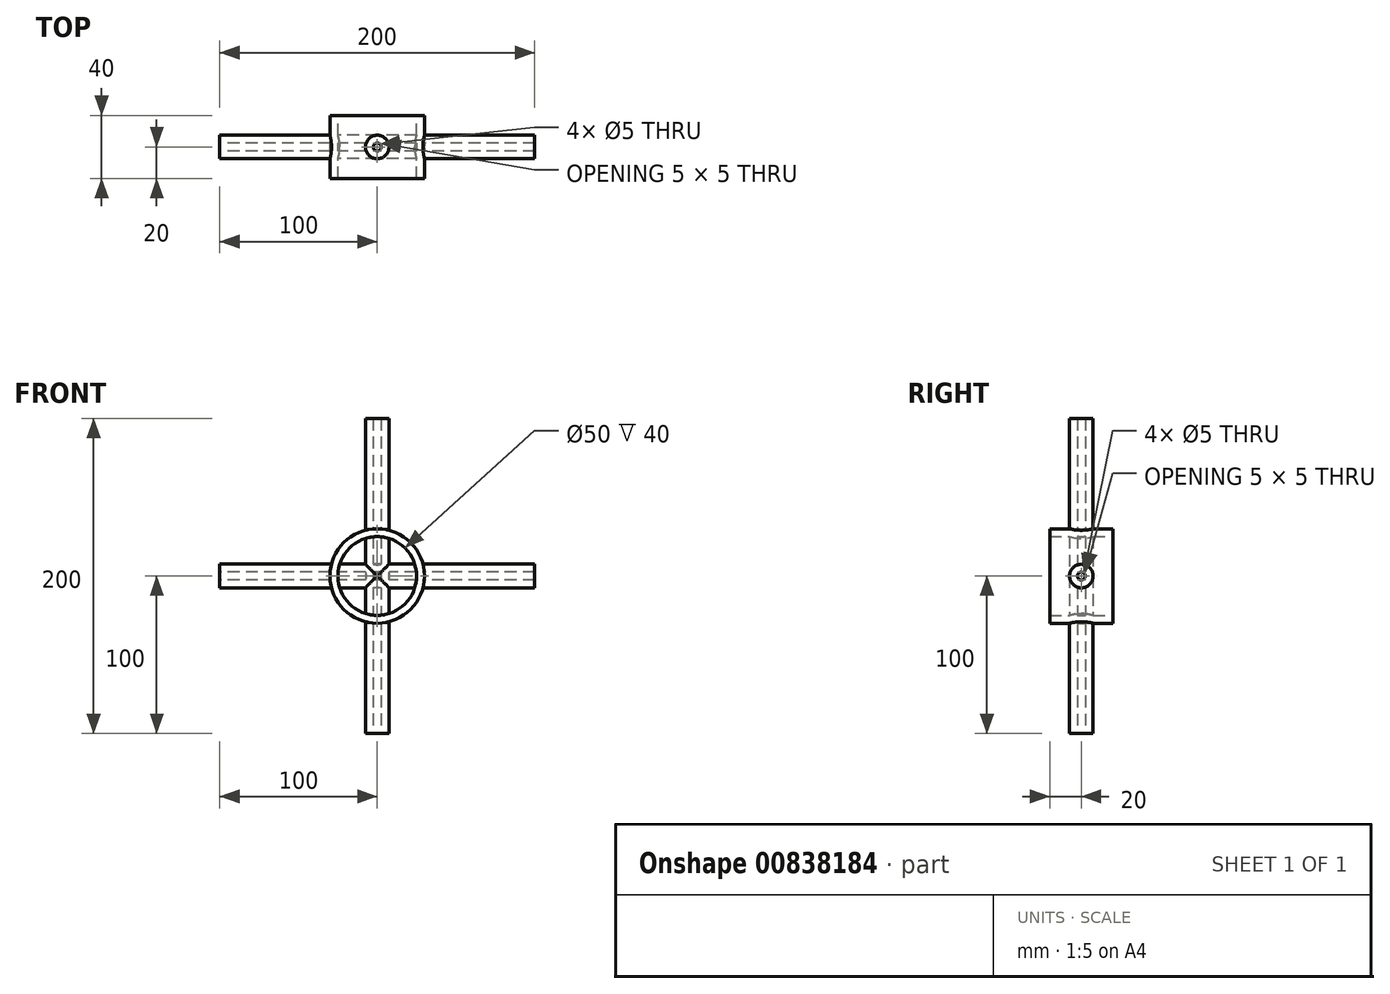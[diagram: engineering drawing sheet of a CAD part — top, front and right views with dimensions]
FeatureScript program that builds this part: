
annotation { "Feature Type Name" : "Feature", "Feature Type Description" : "" }
export const myFeature = defineFeature(function(context is Context, id is Id, definition is map)
    precondition{}
    {
        {
            var Q0;
            Q0=qCreatedBy(makeId("Front.planeOp"),FACE);
            var sketch = newSketch(context, id + "F0", { "sketchPlane" : qUnion([Q0])});
            skCircle(sketch, "E0", {"center": v(0, 0) * mm, "radius": 30 * mm});
            skCircle(sketch, "E1", {"center": v(0, 0) * mm, "radius": 25 * mm});
            skSolve(sketch);
        }
        {
            var Q0;
            Q0 = qSketchRegion(id + "F0", true);
            extrude(context, id + "F1", {"entities" : qUnion([Q0]), "endBound" : BoundingType.SYMMETRIC, "depth" : 40 * mm, "offsetDistance" : 25.4 * mm});
        }
        {
            var Q0;
            Q0=qCreatedBy(makeId("Top.planeOp"),FACE);
            var sketch = newSketch(context, id + "F2", { "sketchPlane" : qUnion([Q0])});
            skCircle(sketch, "E2", {"center": v(0, 0) * mm, "radius": 7.5 * mm});
            skCircle(sketch, "E3", {"center": v(0, 0) * mm, "radius": 2.5 * mm});
            skSolve(sketch);
        }
        {
            var Q0;
            Q0=makeQuery(id+"F2.imprint","IMPRINT",FACE,{"disambiguationData":[TD([[makeQuery(id+"F2.imprint","IMPRINT",EDGE,{"derivedFrom":sQuery(id+"F2.wireOp",EDGE,"E2")}),1.0]])]});
            var Q1;
            Q1=sQuery(id+"F2.wireOp",EDGE,"E3");
            var Q2;
            Q2=sQuery(id+"F2.wireOp",EDGE,"E2");
            extrude(context, id + "F3", {"entities" : qUnion([Q0]), "operationType" : NewBodyOperationType.ADD, "surfaceEntities" : qUnion([Q1, Q2]), "endBound" : BoundingType.SYMMETRIC, "depth" : 200 * mm, "offsetDistance" : 25.4 * mm});
        }
        {
            var Q0;
            Q0=qCreatedBy(makeId("Right.planeOp"),FACE);
            var sketch = newSketch(context, id + "F4", { "sketchPlane" : qUnion([Q0])});
            skCircle(sketch, "E4", {"center": v(0, 0) * mm, "radius": 7.5 * mm});
            skCircle(sketch, "E5", {"center": v(0, 0) * mm, "radius": 2.5 * mm});
            skSolve(sketch);
        }
        {
            var Q0;
            Q0 = qSketchRegion(id + "F4", true);
            extrude(context, id + "F5", {"entities" : qUnion([Q0]), "operationType" : NewBodyOperationType.ADD, "endBound" : BoundingType.SYMMETRIC, "depth" : 200 * mm, "offsetDistance" : 25 * mm});
        }
    });
